# Revit family: Фреоновый охладитель F
name_source: partatom
category: Оборудование
units: mm (PartAtom-declared; Revit-internal decimal feet)

## family parameters
Всегда вертикально = Да
Заголовок OmniClass = Climate Control (HVAC)
На основе рабочей плоскости = Нет
Номер OmniClass = 23.75.00.00
Общий = Нет
При загрузке вырезать с полостями = Нет
Размер круглого соединителя = Использовать диаметр
Тип детали = Нормальный
Точка расчета площади = Нет

## types (8) — shared parameters
ADSK_Единица измерения = шт.
ADSK_Завод-изготовитель = Naveka
ADSK_Наименование = Воздухоохладитель фреоновый
t воздуха на выходе = 16 °C
Материал = RAL 0000 Серый металл
Таблица = Фреоновый охладитель

## per-type parameters (varying)
| type | B | Fн, м2 | H | Vвн | d1 | d2 | s1 | s2 | Аэродинамическое сопротивление | Гидравлическое сопротивление, mbar | Масса | Массовый расход фреона, кг/с | Расход воздуха | Холодопроизводительность |
| F3-5025 | 500 мм | 7.48 м² | 250 мм | 1.4 Л | 12 мм | 15 мм | 20 мм | 112 мм | 92.0 Па | 150 | 7.00 кг | 0.046 | 1152.0 м³/ч | 7000 Вт |
| F3-5030 | 500 мм | 8.98 м² | 300 мм | 1.8 Л | 12 мм | 15 мм | 20 мм | 112 мм | 91.0 Па | 109 | 8.00 кг | 0.054 | 1381.0 м³/ч | 8400 Вт |
| F3-6030 | 600 мм | 10.77 м² | 300 мм | 2.0 Л | 12 мм | 15 мм | 20 мм | 112 мм | 64.0 Па | 178 | 9.00 кг | 0.066 | 1676.0 м³/ч | 10 Вт |
| F3-6035 | 600 мм | 12.57 м² | 350 мм | 2.3 Л | 15 мм | 22 мм | 20 мм | 112 мм | 93.0 Па | 139 | 10.00 кг | 0.077 | 1943.0 м³/ч | 12000 Вт |
| F3-7040 | 700 мм | 16.76 м² | 400 мм | 3.0 Л | 15 мм | 22 мм | 46 мм | 112 мм | 97.0 Па | 190 | 13.00 кг | 0.104 | 2630.0 м³/ч | 16200 Вт |
| F3-8050 | 800 мм | 23.94 м² | 500 мм | 4.4 Л | 22 мм | 28 мм | 30 мм | 112 мм | 95.0 Па | 115 | 17.00 кг | 0.146 | 3695.0 м³/ч | 22600 Вт |
| F3-10050 | 1000 мм | 29.92 м² | 500 мм | 5.3 Л | 22 мм | 28 мм | 40 мм | 122 мм | 97.0 Па | 210 | 21.00 кг | 0.187 | 4619.0 м³/ч | 28000 Вт |
| F3-4020 | 400 мм | 4.79 м² | 200 мм | 1.0 Л | 12 мм | 15 мм | 20 мм | 112 мм | 88.0 Па | 145 | 5.00 кг | 0.022 | 738.0 м³/ч | 4500 Вт |
